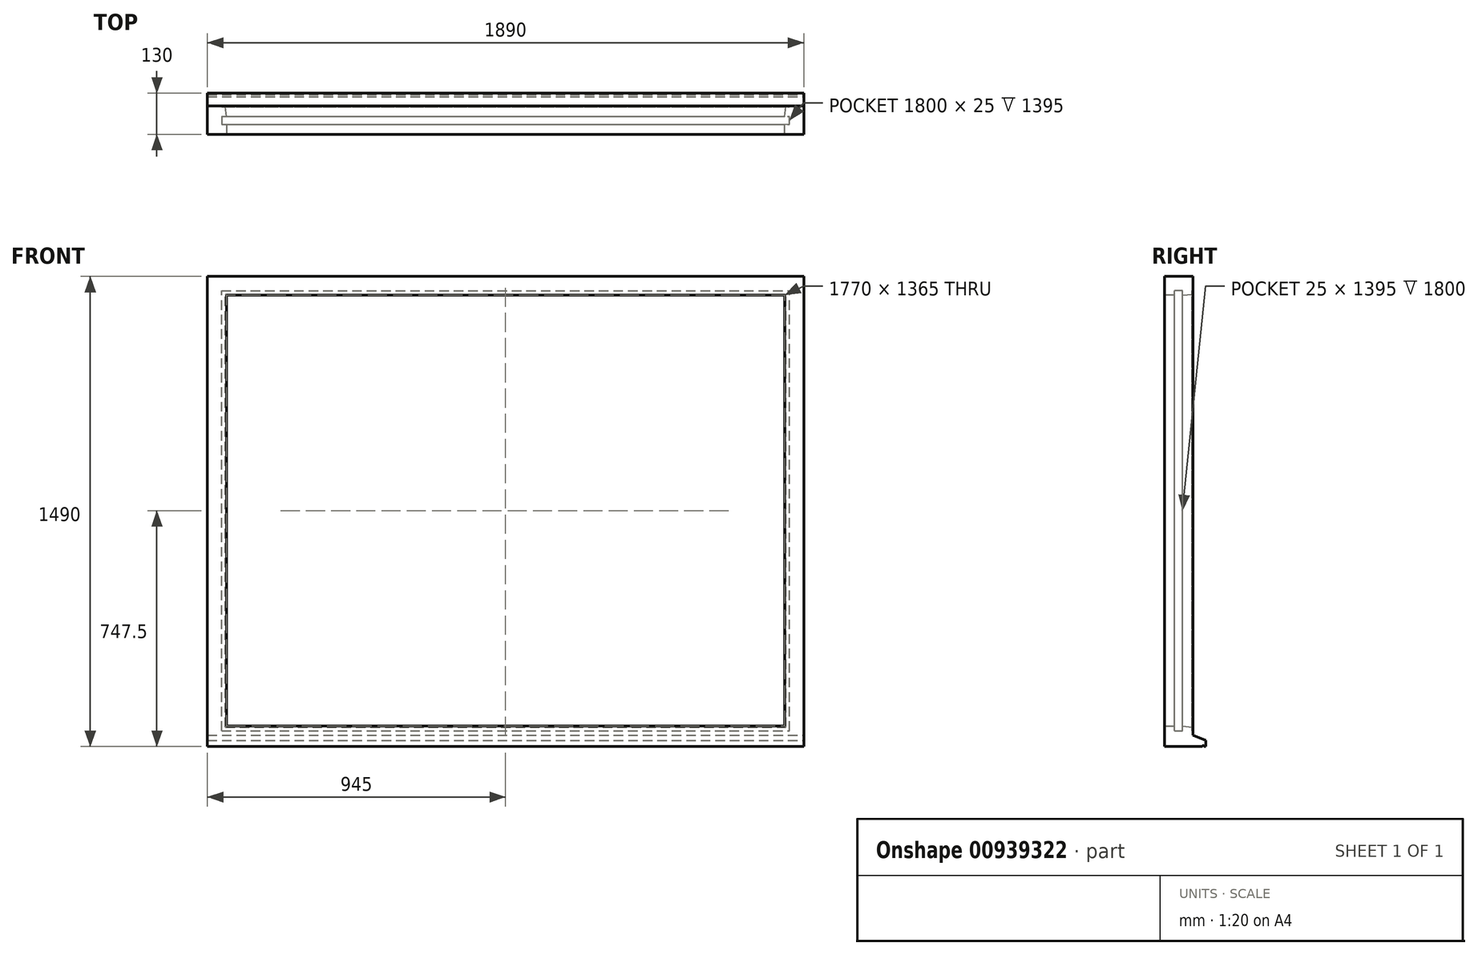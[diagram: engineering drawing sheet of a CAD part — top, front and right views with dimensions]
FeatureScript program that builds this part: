
annotation { "Feature Type Name" : "Feature", "Feature Type Description" : "" }
export const myFeature = defineFeature(function(context is Context, id is Id, definition is map)
    precondition{}
    {
        {
            var Q0;
            Q0=qCreatedBy(makeId("Right.planeOp"),FACE);
            var sketch = newSketch(context, id + "F0", { "sketchPlane" : qUnion([Q0])});
            skLineSegment(sketch, "E0", {"start": v(0, 0) * mm, "end": v(0, 40) * mm});
            skPoint(sketch, "E1.end.orphan", {"position": v(130, 0) * mm});
            skLineSegment(sketch, "E2", {"start": v(130, 20) * mm, "end": v(130, 0) * mm});
            skLineSegment(sketch, "E3", {"start": v(0, 0) * mm, "end": v(119, 0) * mm});
            skArc(sketch, "E4", {"start": v(125, 0) * mm, "mid": v(122, 3) * mm, "end": v(119, 0) * mm});
            skLineSegment(sketch, "E5.trimOffspring", {"start": v(125, 0) * mm, "end": v(130, 0) * mm});
            skLineSegment(sketch, "E6.top", {"start": v(0, 65) * mm, "end": v(32, 65) * mm});
            skLineSegment(sketch, "E6.left", {"start": v(0, 40) * mm, "end": v(0, 65) * mm});
            skLineSegment(sketch, "E6.right", {"start": v(90, 35) * mm, "end": v(90, 50) * mm});
            skLineSegment(sketch, "E7.top", {"start": v(32, 50) * mm, "end": v(90, 50) * mm});
            skLineSegment(sketch, "E7.left", {"start": v(32, 65) * mm, "end": v(32, 50) * mm});
            skPoint(sketch, "E8.start.orphan", {"position": v(90, 35.7) * mm});
            skLineSegment(sketch, "E9", {"start": v(90, 35.7) * mm, "end": v(130, 20) * mm});
            skLineSegment(sketch, "E10", {"start": v(32, 65) * mm, "end": v(0, 65) * mm});
            skLineSegment(sketch, "E11", {"start": v(0, 1490) * mm, "end": v(90, 1490) * mm});
            skLineSegment(sketch, "E12", {"start": v(90, 1490) * mm, "end": v(90, 1445) * mm});
            skLineSegment(sketch, "E13", {"start": v(90, 1445) * mm, "end": v(32, 1445) * mm});
            skLineSegment(sketch, "E14", {"start": v(32, 1445) * mm, "end": v(32, 1430) * mm});
            skLineSegment(sketch, "E15", {"start": v(32, 1430) * mm, "end": v(0, 1430) * mm});
            skLineSegment(sketch, "E16", {"start": v(0, 1430) * mm, "end": v(0, 1490) * mm});
            skLineSegment(sketch, "E17.bottom", {"start": v(87, 1445) * mm, "end": v(57, 1445) * mm});
            skLineSegment(sketch, "E17.left", {"start": v(87, 1445) * mm, "end": v(87, 1433) * mm});
            skLineSegment(sketch, "E17.right", {"start": v(57, 1445) * mm, "end": v(57, 1430) * mm});
            skLineSegment(sketch, "E18", {"start": v(57, 1430) * mm, "end": v(87, 1433) * mm});
            skLineSegment(sketch, "E19", {"start": v(57, 50) * mm, "end": v(87, 50) * mm});
            skLineSegment(sketch, "E20", {"start": v(87, 50) * mm, "end": v(87, 62) * mm});
            skLineSegment(sketch, "E21", {"start": v(57, 65) * mm, "end": v(57, 50) * mm});
            skLineSegment(sketch, "E22", {"start": v(57, 65) * mm, "end": v(87, 62) * mm});
            skSolve(sketch);
        }
        {
            var Q0;
            {var subQ4=sQuery(id+"F0.wireOp",EDGE,"E17.left");var subQ11=sQuery(id+"F0.wireOp",EDGE,"E20");Q0=qUnion([makeQuery(id+"F0.imprint","IMPRINT",FACE,{"disambiguationData":[TD([[makeQuery(id+"F0.imprint","IMPRINT",EDGE,{"derivedFrom":sQuery(id+"F0.wireOp",EDGE,"E0")}),-1.0]])]}),makeQuery(id+"F0.imprint","IMPRINT",FACE,{"disambiguationData":[TD([[makeQuery(id+"F0.imprint","IMPRINT",EDGE,{"derivedFrom":subQ11}),1.0]])]}),makeQuery(id+"F0.imprint","IMPRINT",FACE,{"disambiguationData":[TD([[makeQuery(id+"F0.imprint","IMPRINT",EDGE,{"derivedFrom":subQ4}),-1.0]])]}),makeQuery(id+"F0.imprint","IMPRINT",FACE,{"disambiguationData":[TD([[makeQuery(id+"F0.imprint","IMPRINT",EDGE,{"derivedFrom":sQuery(id+"F0.wireOp",EDGE,"E11")}),-1.0]])]})]);}
            extrude(context, id + "F1", {"entities" : qUnion([Q0]), "oppositeDirection" : true, "depth" : 1890 * mm, "offsetDistance" : 25 * mm});
        }
        {
            var Q0;
            Q0=makeQuery(id+"F1.opExtrude","SWEPT_FACE",FACE,{"disambiguationData":[OSD([sQuery(id+"F0.wireOp",EDGE,"E11")])]});
            var sketch = newSketch(context, id + "F2", { "sketchPlane" : qUnion([Q0])});
            skLineSegment(sketch, "E23", {"start": v(0, 0) * mm, "end": v(0, 90) * mm});
            skLineSegment(sketch, "E24", {"start": v(0, 90) * mm, "end": v(-45, 90) * mm});
            skLineSegment(sketch, "E25", {"start": v(-45, 90) * mm, "end": v(-45, 32) * mm});
            skLineSegment(sketch, "E26", {"start": v(-45, 32) * mm, "end": v(-60, 32) * mm});
            skLineSegment(sketch, "E27", {"start": v(-60, 32) * mm, "end": v(-60, 0) * mm});
            skLineSegment(sketch, "E28", {"start": v(-60, 0) * mm, "end": v(0, 0) * mm});
            skLineSegment(sketch, "E29", {"start": v(-1890, 0) * mm, "end": v(-1830, 0) * mm});
            skLineSegment(sketch, "E30", {"start": v(-1830, 0) * mm, "end": v(-1830, 32) * mm});
            skLineSegment(sketch, "E31", {"start": v(-1830, 32) * mm, "end": v(-1845, 32) * mm});
            skLineSegment(sketch, "E32", {"start": v(-1845, 32) * mm, "end": v(-1845, 90) * mm});
            skLineSegment(sketch, "E33", {"start": v(-1845, 90) * mm, "end": v(-1890, 90) * mm});
            skLineSegment(sketch, "E34", {"start": v(-1890, 90) * mm, "end": v(-1890, 0) * mm});
            skLineSegment(sketch, "E35.bottom", {"start": v(-1845, 87) * mm, "end": v(-1833, 87) * mm});
            skLineSegment(sketch, "E35.top", {"start": v(-1845, 57) * mm, "end": v(-1830, 57) * mm});
            skLineSegment(sketch, "E35.left", {"start": v(-1845, 87) * mm, "end": v(-1845, 57) * mm});
            skLineSegment(sketch, "E36", {"start": v(-1833, 87) * mm, "end": v(-1830, 57) * mm});
            skLineSegment(sketch, "E37.bottom", {"start": v(-45, 57) * mm, "end": v(-60, 57) * mm});
            skLineSegment(sketch, "E37.left", {"start": v(-45, 57) * mm, "end": v(-45, 87) * mm});
            skPoint(sketch, "E37.top.end.orphan", {"position": v(-60, 87) * mm});
            skLineSegment(sketch, "E38", {"start": v(-45, 87) * mm, "end": v(-57, 87) * mm});
            skLineSegment(sketch, "E39", {"start": v(-57, 87) * mm, "end": v(-60, 57) * mm});
            skSolve(sketch);
        }
        {
            var Q0;
            Q0 = qSketchRegion(id + "F2", true);
            extrude(context, id + "F3", {"entities" : qUnion([Q0]), "operationType" : NewBodyOperationType.ADD, "oppositeDirection" : true, "depth" : 1490 * mm, "offsetDistance" : 25 * mm});
        }
    });
